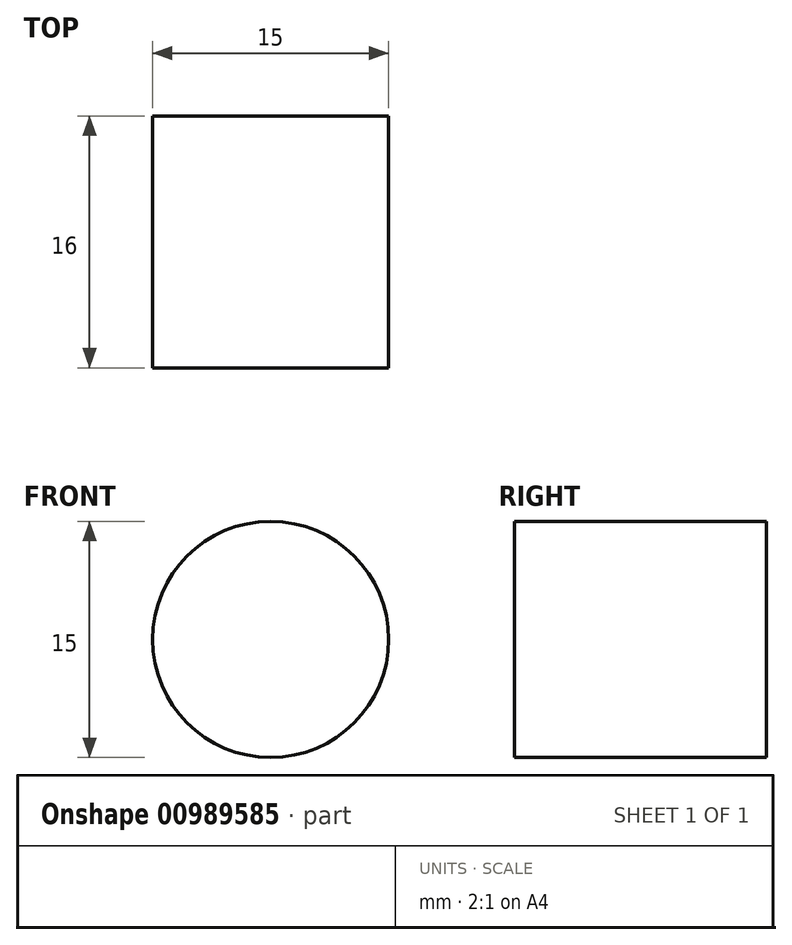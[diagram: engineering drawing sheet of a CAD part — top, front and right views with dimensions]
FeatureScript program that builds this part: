
annotation { "Feature Type Name" : "Feature", "Feature Type Description" : "" }
export const myFeature = defineFeature(function(context is Context, id is Id, definition is map)
    precondition{}
    {
        {
            var Q0;
            Q0=qCreatedBy(makeId("Front.planeOp"),FACE);
            var sketch = newSketch(context, id + "F0", { "sketchPlane" : qUnion([Q0])});
            skCircle(sketch, "E0", {"center": v(0, 0) * mm, "radius": 7.5 * mm});
            skSolve(sketch);
        }
        {
            var Q0;
            Q0 = qSketchRegion(id + "F0", true);
            extrude(context, id + "F1", {"entities" : qUnion([Q0]), "depth" : 16 * mm, "offsetDistance" : 25 * mm});
        }
    });
